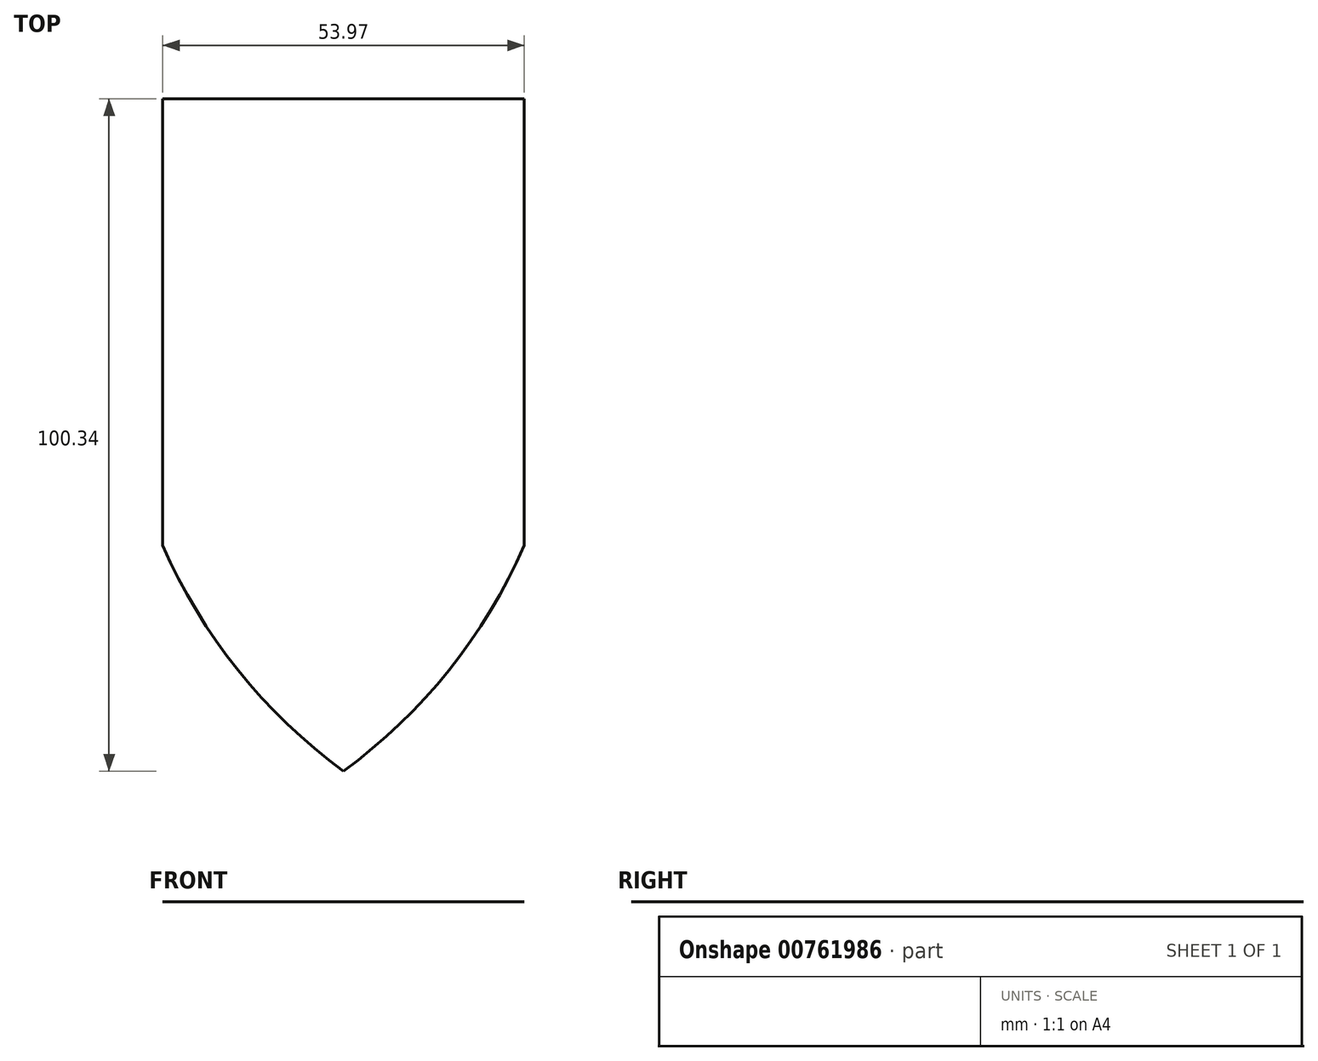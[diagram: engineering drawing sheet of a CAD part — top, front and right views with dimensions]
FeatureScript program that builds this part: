
annotation { "Feature Type Name" : "Feature", "Feature Type Description" : "" }
export const myFeature = defineFeature(function(context is Context, id is Id, definition is map)
    precondition{}
    {
        {
            var Q0;
            Q0=qCreatedBy(makeId("Top.planeOp"),FACE);
            var sketch = newSketch(context, id + "F0", { "sketchPlane" : qUnion([Q0])});
            skLineSegment(sketch, "E0", {"start": v(-23.13, 51.72) * mm, "end": v(-23.13, -14.96) * mm});
            skLineSegment(sketch, "E1", {"start": v(30.84, 51.72) * mm, "end": v(30.84, -14.96) * mm});
            skLineSegment(sketch, "E2", {"start": v(-23.13, 51.72) * mm, "end": v(30.84, 51.72) * mm});
            skArc(sketch, "E3", {"start": v(-23.13, -14.96) * mm, "mid": v(-11.87, -33.58) * mm, "end": v(3.86, -48.62) * mm});
            skArc(sketch, "E4", {"start": v(3.86, -48.62) * mm, "mid": v(19.59, -33.58) * mm, "end": v(30.84, -14.96) * mm});
            skSolve(sketch);
        }
        {
            var Q0;
            Q0=makeQuery(id+"F0.imprint","IMPRINT",FACE,{"disambiguationData":[TD([[makeQuery(id+"F0.imprint","IMPRINT",EDGE,{"derivedFrom":sQuery(id+"F0.wireOp",EDGE,"E0")}),1.0]])]});
            extrude(context, id + "F1", {"entities" : qUnion([Q0]), "depth" : 1 / 203.2 * mm, "offsetDistance" : 25.4 * mm});
        }
    });
